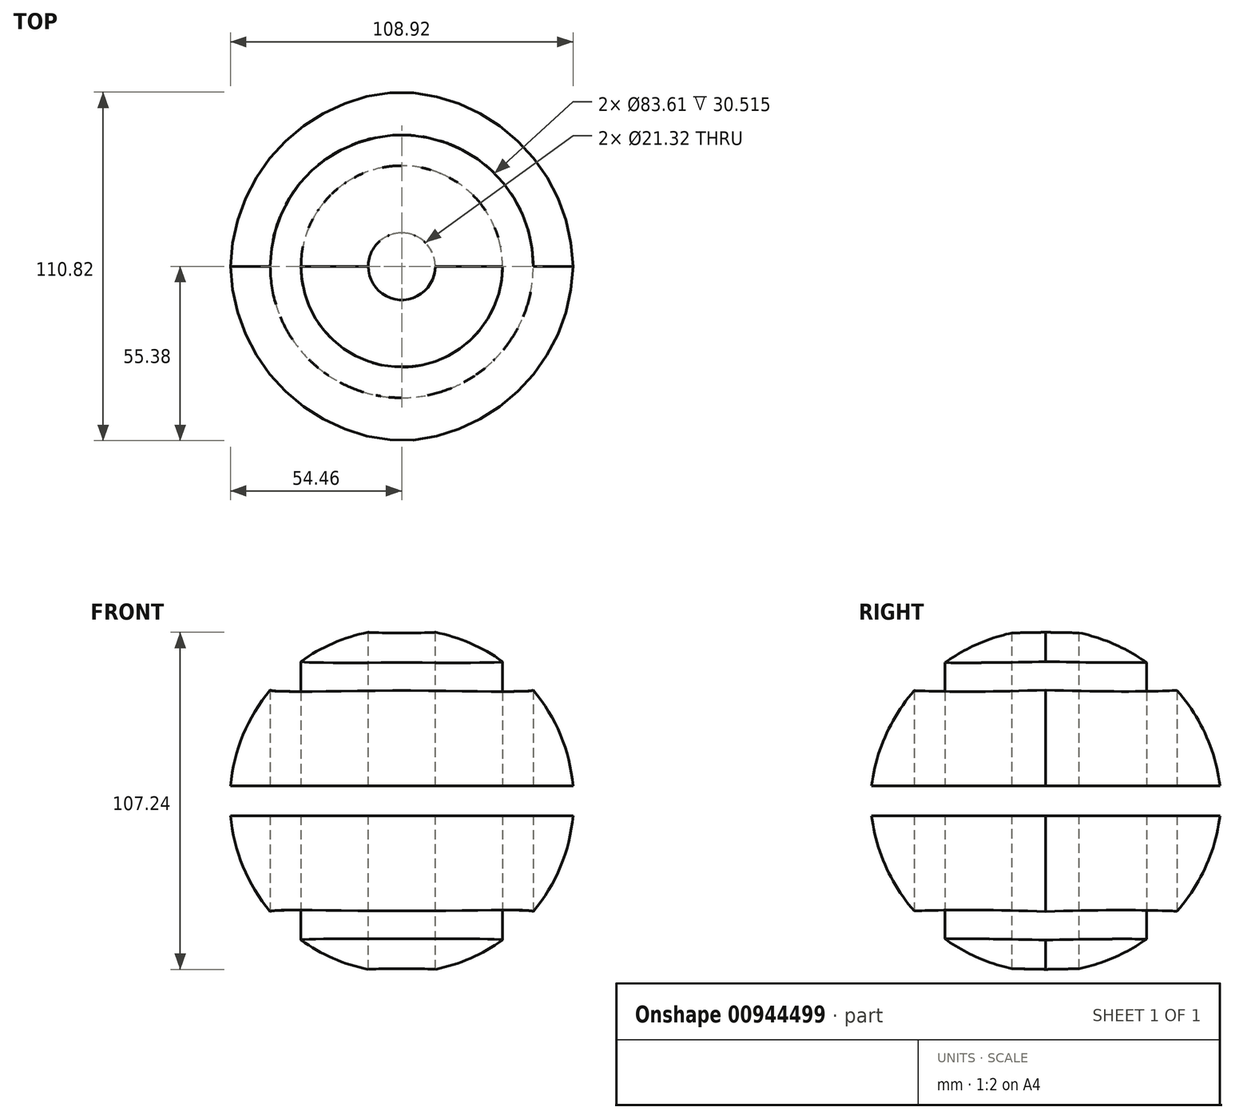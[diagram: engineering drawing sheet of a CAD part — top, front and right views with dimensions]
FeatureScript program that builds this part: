
annotation { "Feature Type Name" : "Feature", "Feature Type Description" : "" }
export const myFeature = defineFeature(function(context is Context, id is Id, definition is map)
    precondition{}
    {
        {
            var Q0;
            Q0=qCreatedBy(makeId("Top.planeOp"),FACE);
            var sketch = newSketch(context, id + "F0", { "sketchPlane" : qUnion([Q0])});
            skArc(sketch, "E0", {"start": v(54.67, 0) * mm, "mid": v(38.37, 38.73) * mm, "end": v(0, 55.84) * mm});
            skArc(sketch, "E1", {"start": v(0, -55.78) * mm, "mid": v(38.35, -38.69) * mm, "end": v(54.67, 0) * mm});
            skArc(sketch, "E2.0", {"start": v(67.11, 0.27) * mm, "mid": v(47.26, 47.43) * mm, "end": v(0.54, 68.28) * mm});
            skArc(sketch, "E3.0", {"start": v(0.55, -68.47) * mm, "mid": v(47.42, -47.58) * mm, "end": v(67.36, -0.3) * mm});
            skLineSegment(sketch, "E4", {"start": v(0, 55.84) * mm, "end": v(0, -55.78) * mm});
            skSolve(sketch);
        }
        {
            var Q0;
            Q0=makeQuery(id+"F0.imprint","IMPRINT",FACE,{"disambiguationData":[TD([[makeQuery(id+"F0.imprint","IMPRINT",EDGE,{"derivedFrom":sQuery(id+"F0.wireOp",EDGE,"E0")}),1.0]])]});
            var Q1;
            Q1=sQuery(id+"F0.wireOp",EDGE,"E4");
            revolve(context, id + "F1", {"surfaceOperationType" : NewSurfaceOperationType.NEW, "entities" : qUnion([Q0]), "axis" : qUnion([Q1]), "revolveType" : RevolveType.FULL});
        }
        {
            var Q0;
            Q0=qCreatedBy(makeId("Top.planeOp"),FACE);
            var sketch = newSketch(context, id + "F2", { "sketchPlane" : qUnion([Q0])});
            skCircle(sketch, "E5", {"center": v(0, 0) * mm, "radius": 10.66 * mm});
            skSolve(sketch);
        }
        {
            var Q0;
            Q0 = qSketchRegion(id + "F2", true);
            extrude(context, id + "F3", {"entities" : qUnion([Q0]), "operationType" : NewBodyOperationType.REMOVE, "endBound" : BoundingType.SYMMETRIC, "oppositeDirection" : true, "depth" : 254 * mm, "offsetDistance" : 25.4 * mm});
        }
        {
            var Q0;
            Q0=qCreatedBy(makeId("Top.planeOp"),FACE);
            var sketch = newSketch(context, id + "F4", { "sketchPlane" : qUnion([Q0])});
            skCircle(sketch, "E6", {"center": v(0, 0) * mm, "radius": 41.8 * mm});
            skCircle(sketch, "E7", {"center": v(0, 0) * mm, "radius": 32.03 * mm});
            skSolve(sketch);
        }
        {
            var Q0;
            Q0 = qSketchRegion(id + "F4", true);
            extrude(context, id + "F5", {"entities" : qUnion([Q0]), "operationType" : NewBodyOperationType.REMOVE, "endBound" : BoundingType.SYMMETRIC, "depth" : 203.2 * mm, "offsetDistance" : 25.4 * mm});
        }
        {
            var Q0;
            Q0=qCreatedBy(makeId("Right.planeOp"),FACE);
            var sketch = newSketch(context, id + "F6", { "sketchPlane" : qUnion([Q0])});
            skLineSegment(sketch, "E8.bottom", {"start": v(60.9, 4.71) * mm, "end": v(-60.9, 4.71) * mm});
            skLineSegment(sketch, "E8.top", {"start": v(60.9, -4.71) * mm, "end": v(-60.9, -4.71) * mm});
            skLineSegment(sketch, "E8.left", {"start": v(60.9, 4.71) * mm, "end": v(60.9, -4.71) * mm});
            skLineSegment(sketch, "E8.right", {"start": v(-60.9, 4.71) * mm, "end": v(-60.9, -4.71) * mm});
            skPoint(sketch, "E8.middle", {"position": v(0, 0) * mm});
            skSolve(sketch);
        }
        {
            var Q0;
            Q0 = qSketchRegion(id + "F6", true);
            extrude(context, id + "F7", {"entities" : qUnion([Q0]), "operationType" : NewBodyOperationType.REMOVE, "endBound" : BoundingType.SYMMETRIC, "oppositeDirection" : true, "depth" : 254 * mm, "offsetDistance" : 25.4 * mm});
        }
    });
